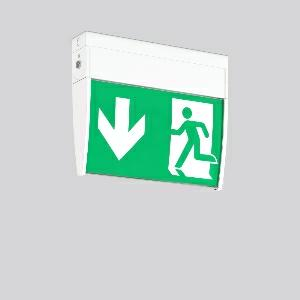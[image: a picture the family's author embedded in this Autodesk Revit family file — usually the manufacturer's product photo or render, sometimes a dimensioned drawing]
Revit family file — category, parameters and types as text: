
# Revit family: gsun_d_671996_002_2_bbd5
name_source: partatom
category: Lighting Fixtures
units: mm (PartAtom-declared; Revit-internal decimal feet)

## family parameters
Cut with Voids When Loaded = No
Host = Face
Light Source = No
Part Type = Normal
Room Calculation Point = No
Round Connector Dimension = Use Diameter
Shared = No

## types (1)
- GSUN D
    Apparent Load = 0 VA
    Default Elevation = 1800 mm
    Description = Series: GSUN D
Luminaire for escape route identification. Housing: extruded aluminium profile, powder-coated. 4 legends and 1 white lay in plastic sheet included. Universal mounting kit for ceiling and wall surface mounting. Driver integrated. Suitable for connection to central battery systems. 
Colour: white
Length: 247 mm
Width: 45 mm
Height: 200 mm
Weight: 1 kg
Operating mode: maintained power mode
Viewing Distance: 24 m
Lamp: LED
Socket: without socket
Colour temperature: 4000K
System power: 3.7 W
System power, emergency: 3.7 W
Control gear: Converter not necessary
Protection class: I
Type of protection: IP 30
    Height = 200 mm  [stored 0.656168 ft]
    Lamp = 0 x
    Length = 247 mm
    Luminous efficacy = 0 lm/W
    Manufacturer = RZB
    ModVariant = No
    Model = 671996.002.2
    Mounting Place = Ceiling, Wall
    Mounting Type = Surface mounted
    Number of Poles = 1
    OnlyDefault = Yes
    Power Factor = 1
    Product Name = GSUN D
    Product group = Surface mounted ceiling and wall luminaires
    ProductGroupID = 305
    Protection Class = Protection class I
    Protection Degree = IP 30
    RLX_Detail_Level = 1
    RLX_Emergency_Light_Flux = 0 lm
    RLX_Emergency_Type = 0
    RLX_Emergency_Type_DB = No
    RlxData = <blob elided: 31881 chars, md5=4e14a93f>
    Standby Power = 0 W
    System Light Flux = 0 lm
    System Power = 0 W
    Type Comments = Product without accessories
    Type Image = 652219.002.jpg
    URL = http://relux.com
    VarID = ---
    Voltage = 230 V
    Voltage Range = 220-240 V
    Weight = 0.00 kg
    Width = 45 mm

note: [stored X ft] marks values corroborated as IEEE doubles in the binary element streams (Revit-internal decimal feet)

## geometry (parser evidence)
native form markers: Blend x4, Sweep x9
no freeform markers — native parametric forms only
